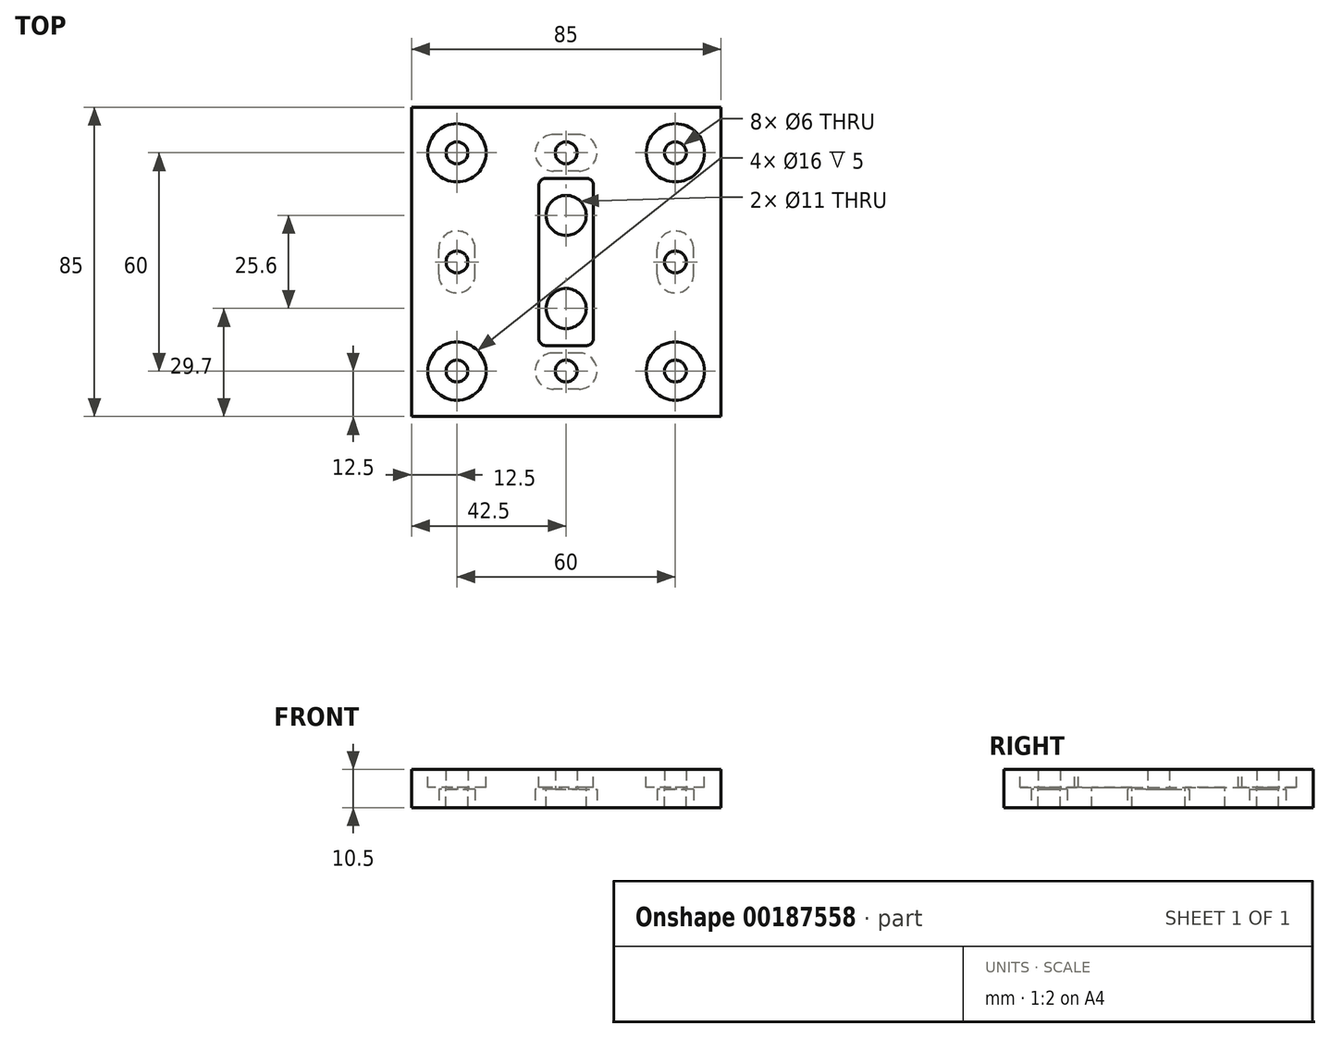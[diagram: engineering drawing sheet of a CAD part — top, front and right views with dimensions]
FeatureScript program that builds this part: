
annotation { "Feature Type Name" : "Feature", "Feature Type Description" : "" }
export const myFeature = defineFeature(function(context is Context, id is Id, definition is map)
    precondition{}
    {
        {
            var Q0;
            Q0=qCreatedBy(makeId("Top.planeOp"),FACE);
            var sketch = newSketch(context, id + "F0", { "sketchPlane" : qUnion([Q0])});
            skLineSegment(sketch, "E0.bottom", {"start": v(42.5, 42.5) * mm, "end": v(-42.5, 42.5) * mm});
            skLineSegment(sketch, "E0.top", {"start": v(42.5, -42.5) * mm, "end": v(-42.5, -42.5) * mm});
            skLineSegment(sketch, "E0.left", {"start": v(42.5, 42.5) * mm, "end": v(42.5, -42.5) * mm});
            skLineSegment(sketch, "E0.right", {"start": v(-42.5, 42.5) * mm, "end": v(-42.5, -42.5) * mm});
            skPoint(sketch, "E0.middle", {"position": v(0, 0) * mm});
            skSolve(sketch);
        }
        {
            var Q0;
            Q0=makeQuery(id+"F0.imprint","IMPRINT",FACE,{"disambiguationData":[TD([[makeQuery(id+"F0.imprint","IMPRINT",EDGE,{"derivedFrom":sQuery(id+"F0.wireOp",EDGE,"E0.bottom")}),1.0]])]});
            extrude(context, id + "F1", {"entities" : qUnion([Q0]), "depth" : 10.5 * mm});
        }
        {
            var Q0;
            Q0=makeQuery(id+"F1.opExtrude","CAP_FACE",FACE,{"disambiguationData":[OSD([sQuery(id+"F0.wireOp",EDGE,"E0.bottom"),sQuery(id+"F0.wireOp",EDGE,"E0.top"),sQuery(id+"F0.wireOp",EDGE,"E0.left"),sQuery(id+"F0.wireOp",EDGE,"E0.right")])],"isStart":false});
            var sketch = newSketch(context, id + "F2", { "sketchPlane" : qUnion([Q0])});
            skLineSegment(sketch, "E1", {"start": v(0, 42.5) * mm, "end": v(0, -42.5) * mm, "construction": true});
            skCircle(sketch, "E2", {"center": v(0, 12.8) * mm, "radius": 5.5 * mm});
            skCircle(sketch, "E3.MirrorC", {"center": v(0, -12.8) * mm, "radius": 5.5 * mm});
            skSolve(sketch);
        }
        {
            var Q0;
            Q0 = qSketchRegion(id + "F2", true);
            extrude(context, id + "F3", {"entities" : qUnion([Q0]), "operationType" : NewBodyOperationType.REMOVE, "endBound" : BoundingType.THROUGH_ALL, "oppositeDirection" : true, "depth" : 25 * mm});
        }
        {
            var Q0;
            Q0=makeQuery(id+"F1.opExtrude","CAP_FACE",FACE,{"disambiguationData":[OSD([sQuery(id+"F0.wireOp",EDGE,"E0.bottom"),sQuery(id+"F0.wireOp",EDGE,"E0.top"),sQuery(id+"F0.wireOp",EDGE,"E0.left"),sQuery(id+"F0.wireOp",EDGE,"E0.right")])],"isStart":false});
            var sketch = newSketch(context, id + "F4", { "sketchPlane" : qUnion([Q0])});
            skLineSegment(sketch, "E4.bottom", {"start": v(5.5, -23) * mm, "end": v(-5.5, -23) * mm});
            skLineSegment(sketch, "E4.top", {"start": v(5.5, 23) * mm, "end": v(-5.5, 23) * mm});
            skLineSegment(sketch, "E4.left", {"start": v(7.5, -21) * mm, "end": v(7.5, 21) * mm});
            skLineSegment(sketch, "E4.right", {"start": v(-7.5, -21) * mm, "end": v(-7.5, 21) * mm});
            skPoint(sketch, "E4.middle", {"position": v(0, 0) * mm});
            skPoint(sketch, "E5.visualSharp", {"position": v(-7.5, 23) * mm});
            skArc(sketch, "E5.filletArc", {"start": v(-5.5, 23) * mm, "mid": v(-6.91, 22.41) * mm, "end": v(-7.5, 21) * mm});
            skPoint(sketch, "E6.visualSharp", {"position": v(7.5, 23) * mm});
            skArc(sketch, "E6.filletArc", {"start": v(7.5, 21) * mm, "mid": v(6.91, 22.41) * mm, "end": v(5.5, 23) * mm});
            skPoint(sketch, "E7.visualSharp", {"position": v(7.5, -23) * mm});
            skArc(sketch, "E7.filletArc", {"start": v(5.5, -23) * mm, "mid": v(6.91, -22.41) * mm, "end": v(7.5, -21) * mm});
            skPoint(sketch, "E8.visualSharp", {"position": v(-7.5, -23) * mm});
            skArc(sketch, "E8.filletArc", {"start": v(-7.5, -21) * mm, "mid": v(-6.91, -22.41) * mm, "end": v(-5.5, -23) * mm});
            skSolve(sketch);
        }
        {
            var Q0;
            Q0 = qSketchRegion(id + "F4", true);
            extrude(context, id + "F5", {"entities" : qUnion([Q0]), "operationType" : NewBodyOperationType.REMOVE, "oppositeDirection" : true, "depth" : 5 * mm});
        }
        {
            var Q0;
            Q0=makeQuery(id+"F1.opExtrude","CAP_FACE",FACE,{"disambiguationData":[OSD([sQuery(id+"F0.wireOp",EDGE,"E0.bottom"),sQuery(id+"F0.wireOp",EDGE,"E0.top"),sQuery(id+"F0.wireOp",EDGE,"E0.left"),sQuery(id+"F0.wireOp",EDGE,"E0.right")])],"isStart":false});
            var sketch = newSketch(context, id + "F6", { "sketchPlane" : qUnion([Q0])});
            skLineSegment(sketch, "E9", {"start": v(-42.5, 0) * mm, "end": v(42.5, 0) * mm, "construction": true});
            skLineSegment(sketch, "E10.bottom", {"start": v(30, 30) * mm, "end": v(-30, 30) * mm, "construction": true});
            skLineSegment(sketch, "E10.top", {"start": v(30, -30) * mm, "end": v(-30, -30) * mm, "construction": true});
            skLineSegment(sketch, "E10.left", {"start": v(30, 30) * mm, "end": v(30, -30) * mm, "construction": true});
            skLineSegment(sketch, "E10.right", {"start": v(-30, 30) * mm, "end": v(-30, -30) * mm, "construction": true});
            skPoint(sketch, "E10.middle", {"position": v(0, 0) * mm});
            skCircle(sketch, "E11", {"center": v(-30, 30) * mm, "radius": 8.25 * mm, "construction": true});
            skCircle(sketch, "E12", {"center": v(30, 30) * mm, "radius": 8.25 * mm, "construction": true});
            skCircle(sketch, "E13", {"center": v(30, -30) * mm, "radius": 8.25 * mm, "construction": true});
            skCircle(sketch, "E14", {"center": v(-30, -30) * mm, "radius": 8.25 * mm, "construction": true});
            skCircle(sketch, "E15", {"center": v(30, 30) * mm, "radius": 8 * mm});
            skCircle(sketch, "E16", {"center": v(30, -30) * mm, "radius": 8 * mm});
            skCircle(sketch, "E17", {"center": v(-30, -30) * mm, "radius": 8 * mm});
            skCircle(sketch, "E18", {"center": v(-30, 30) * mm, "radius": 8 * mm});
            skSolve(sketch);
        }
        {
            var Q0;
            Q0 = qSketchRegion(id + "F6", true);
            extrude(context, id + "F7", {"entities" : qUnion([Q0]), "operationType" : NewBodyOperationType.REMOVE, "oppositeDirection" : true, "depth" : 5 * mm});
        }
        {
            var Q0;
            Q0=sQuery(id+"F6.wireOp",VERTEX,"E10.top.end");
            var Q1;
            Q1=sQuery(id+"F6.wireOp",VERTEX,"E10.left.end");
            var Q2;
            Q2=sQuery(id+"F6.wireOp",VERTEX,"E10.left.start");
            var Q3;
            Q3=sQuery(id+"F6.wireOp",VERTEX,"E10.bottom.end");
            var Q4;
            Q4=makeQuery(id+"F1.opExtrude","SWEPT_BODY",BODY,{"disambiguationData":[OSD([sQuery(id+"F0.wireOp",EDGE,"E0.bottom"),sQuery(id+"F0.wireOp",EDGE,"E0.top"),sQuery(id+"F0.wireOp",EDGE,"E0.left"),sQuery(id+"F0.wireOp",EDGE,"E0.right")])]});
            hole(context, id + "F8", {"style" : HoleStyle.SIMPLE, "endStyle" : HoleEndStyle.THROUGH, "holeDiameter" : 6 * mm, "locations" : qUnion([Q0, Q1, Q2, Q3]), "scope" : qUnion([Q4]), "isTappedThrough" : true});
        }
        {
            var Q0;
            Q0=makeQuery(id+"F1.opExtrude","CAP_FACE",FACE,{"disambiguationData":[OSD([sQuery(id+"F0.wireOp",EDGE,"E0.bottom"),sQuery(id+"F0.wireOp",EDGE,"E0.top"),sQuery(id+"F0.wireOp",EDGE,"E0.left"),sQuery(id+"F0.wireOp",EDGE,"E0.right")])],"isStart":true});
            var sketch = newSketch(context, id + "F9", { "sketchPlane" : qUnion([Q0])});
            skLineSegment(sketch, "E19.0", {"start": v(-30, -30) * mm, "end": v(-30, 30) * mm, "construction": true});
            skLineSegment(sketch, "E20.0", {"start": v(30, 30) * mm, "end": v(-30, 30) * mm, "construction": true});
            skLineSegment(sketch, "E21.0", {"start": v(30, -30) * mm, "end": v(30, 30) * mm, "construction": true});
            skLineSegment(sketch, "E22.0", {"start": v(30, -30) * mm, "end": v(-30, -30) * mm, "construction": true});
            skLineSegment(sketch, "E23", {"start": v(-42.5, 0) * mm, "end": v(42.5, 0) * mm, "construction": true});
            skLineSegment(sketch, "E24", {"start": v(0, 42.5) * mm, "end": v(0, -42.5) * mm, "construction": true});
            skLineSegment(sketch, "E25", {"start": v(30, 3.5) * mm, "end": v(30, -3.5) * mm, "construction": true});
            skArc(sketch, "E26.0.startCap", {"start": v(25, 3.5) * mm, "mid": v(30, 8.5) * mm, "end": v(35, 3.5) * mm});
            skArc(sketch, "E26.0.endCap", {"start": v(35, -3.5) * mm, "mid": v(30, -8.5) * mm, "end": v(25, -3.5) * mm});
            skLineSegment(sketch, "E26.0.left", {"start": v(35, 3.5) * mm, "end": v(35, -3.5) * mm});
            skLineSegment(sketch, "E26.0.right", {"start": v(25, 3.5) * mm, "end": v(25, -3.5) * mm});
            skPoint(sketch, "E27", {"position": v(30, 0) * mm});
            skLineSegment(sketch, "E28", {"start": v(3.5, 30) * mm, "end": v(-3.5, 30) * mm, "construction": true});
            skArc(sketch, "E29.0.startCap", {"start": v(3.5, 35) * mm, "mid": v(8.5, 30) * mm, "end": v(3.5, 25) * mm});
            skArc(sketch, "E29.0.endCap", {"start": v(-3.5, 25) * mm, "mid": v(-8.5, 30) * mm, "end": v(-3.5, 35) * mm});
            skLineSegment(sketch, "E29.0.left", {"start": v(3.5, 25) * mm, "end": v(-3.5, 25) * mm});
            skLineSegment(sketch, "E29.0.right", {"start": v(3.5, 35) * mm, "end": v(-3.5, 35) * mm});
            skArc(sketch, "E30.MirrorCS", {"start": v(35, 3.5) * mm, "mid": v(30, 8.5) * mm, "end": v(25, 3.5) * mm});
            skArc(sketch, "E31.MirrorCS", {"start": v(25, -3.5) * mm, "mid": v(30, -8.5) * mm, "end": v(35, -3.5) * mm});
            skPoint(sketch, "E32.MirrorP", {"position": v(-30, 0) * mm});
            skArc(sketch, "E33.MirrorCS", {"start": v(-35, 3.5) * mm, "mid": v(-30, 8.5) * mm, "end": v(-25, 3.5) * mm});
            skArc(sketch, "E34.MirrorCS", {"start": v(-35, -3.5) * mm, "mid": v(-30, -8.5) * mm, "end": v(-25, -3.5) * mm});
            skLineSegment(sketch, "E35.MirrorCS", {"start": v(-35, 3.5) * mm, "end": v(-35, -3.5) * mm});
            skLineSegment(sketch, "E36.MirrorCS", {"start": v(-25, 3.5) * mm, "end": v(-25, -3.5) * mm});
            skArc(sketch, "E37.MirrorCS", {"start": v(-25, 3.5) * mm, "mid": v(-30, 8.5) * mm, "end": v(-35, 3.5) * mm});
            skLineSegment(sketch, "E38.MirrorCS", {"start": v(-30, 3.5) * mm, "end": v(-30, -3.5) * mm, "construction": true});
            skArc(sketch, "E39.MirrorCS", {"start": v(-25, -3.5) * mm, "mid": v(-30, -8.5) * mm, "end": v(-35, -3.5) * mm});
            skPoint(sketch, "E40", {"position": v(0, 30) * mm});
            skLineSegment(sketch, "E41.MirrorCS", {"start": v(3.5, -35) * mm, "end": v(-3.5, -35) * mm});
            skLineSegment(sketch, "E42.MirrorCS", {"start": v(3.5, -30) * mm, "end": v(-3.5, -30) * mm, "construction": true});
            skLineSegment(sketch, "E43.MirrorCS", {"start": v(3.5, -25) * mm, "end": v(-3.5, -25) * mm});
            skPoint(sketch, "E44.MirrorP", {"position": v(0, -30) * mm});
            skArc(sketch, "E45.MirrorCS", {"start": v(-3.5, -25) * mm, "mid": v(-8.5, -30) * mm, "end": v(-3.5, -35) * mm});
            skArc(sketch, "E46.MirrorCS", {"start": v(3.5, -35) * mm, "mid": v(8.5, -30) * mm, "end": v(3.5, -25) * mm});
            skSolve(sketch);
        }
        {
            var Q0;
            Q0 = qSketchRegion(id + "F9", true);
            extrude(context, id + "F10", {"entities" : qUnion([Q0]), "operationType" : NewBodyOperationType.REMOVE, "oppositeDirection" : true, "depth" : 5 * mm});
        }
        {
            var Q0;
            Q0=makeQuery(id+"F1.opExtrude","CAP_FACE",FACE,{"disambiguationData":[OSD([sQuery(id+"F0.wireOp",EDGE,"E0.bottom"),sQuery(id+"F0.wireOp",EDGE,"E0.top"),sQuery(id+"F0.wireOp",EDGE,"E0.left"),sQuery(id+"F0.wireOp",EDGE,"E0.right")])],"isStart":true});
            var sketch = newSketch(context, id + "F11", { "sketchPlane" : qUnion([Q0])});
            skCircle(sketch, "E47", {"center": v(0, 30) * mm, "radius": 3 * mm});
            skPoint(sketch, "E47.centerSnap0", {"position": v(0, 35) * mm});
            skPoint(sketch, "E47.centerSnap1", {"position": v(8.5, 30) * mm});
            skCircle(sketch, "E48.MirrorC", {"center": v(0, -30) * mm, "radius": 3 * mm});
            skCircle(sketch, "E49", {"center": v(30, 0) * mm, "radius": 3 * mm});
            skPoint(sketch, "E49.centerSnap0", {"position": v(30, 8.5) * mm});
            skCircle(sketch, "E50.MirrorC", {"center": v(-30, 0) * mm, "radius": 3 * mm});
            skSolve(sketch);
        }
        {
            var Q0;
            Q0 = qSketchRegion(id + "F11", true);
            extrude(context, id + "F12", {"entities" : qUnion([Q0]), "operationType" : NewBodyOperationType.REMOVE, "oppositeDirection" : true, "depth" : 25 * mm});
        }
    });
